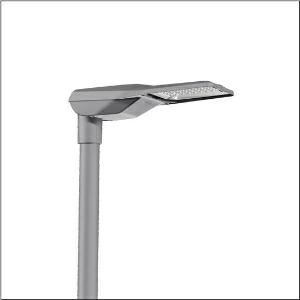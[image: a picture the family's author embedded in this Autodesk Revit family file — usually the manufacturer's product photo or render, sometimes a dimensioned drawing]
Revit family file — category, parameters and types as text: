
# Revit family: streetlight_sl_21_iq_mini___stw1_0a_5xe2e31d08hb_6dd6
name_source: partatom
category: Lighting Fixtures
units: mm (PartAtom-declared; Revit-internal decimal feet)

## family parameters
Cut with Voids When Loaded = No
Host = Face
Light Source = No
Part Type = Normal
Room Calculation Point = No
Round Connector Dimension = Use Diameter
Shared = No

## types (1)
- --- (1 x LED, 9450 lm, 70.9 W, 3000K)
    Apparent Load = 71 VA
    CIE Flux Codes = 38 75 98 100 100
    Color Rendering = 70
    Color Temperature = 3000K
    Default Elevation = 1800 mm
    Description = Streetlight SL 21 iQ mini, mast luminaire, primary light control with lens, of PMMA, primary optical cover: cover, of toughened safety glass, transparent, light distribution: STW1.0a, light emission: direct distribution, primary light characteristic: asymmetric, installation type: post-top, side-entry, LED, High Power LED, rated luminous flux: 9.450lm, luminous efficacy: 133lm/W, light colour: 730, colour temperature: 3000K, control: Auto-Match, Temp-Guard, Lumen-Switch, Night-Set, Smart-Wire, Light-Fading, Desk-Remote (wireless, voltage-free reading and setting of iQ features in the workshop via application-optimized NFC function/RFID function), optimised constant luminous flux control (CLO 2.0), pre-setting: linear dimming characteristic, mains connection: 220..240V, AC, 50/60Hz, start of lifetime: 71W, end of service life: 75W, reduction: 31W, luminaire housing, of diecast aluminium, powder-coated, Siteco® metallic grey (DB 702S), corrosivity category C5 mid according to DIN EN ISO 12944, please order mast flange separately, inclination adjustable: 0°, 5°, 10°, 15°, sealing non-destructively replaceable, multi-level sealing system, length: 628mm, width: 235mm, height: 110mm, mast flange for spigot size: 42mm (side-entry): 5XC10008XM4, 60/48mm (side-entry/post-top): 5XC10108XM2, 76/60mm (side-entry/post-top): 5XC10108XM1, protection rating (complete): IP66, insulation class (complete): insulation class II (safety insulation), certification: CE, ENEC, ENEC+, VDE, impact resistance: IK09, permissible operating ambient temperature for outdoor applications: -40..+50°C, standard-compliant lighting for roads and squares, packaging unit: 1 piece

Light Distribution: STW1.0a
    Height = 110 mm
    Lamp = 1 x LED
    Lamp Light Flux = 9450 lm
    Lamp Power = 70.9 W
    Lamp count = 1
    Length = 625 mm
    Luminous efficacy = 133 lm/W
    Manufacturer = Siteco
    ModVariant = No
    Model = 5XE2E31D08HB
    Number of Poles = 1
    OnlyDefault = Yes
    Power Factor = 1
    Product Name = Streetlight SL 21 iQ mini | STW1.0a
    Product group = mast luminaire | pylon top
    ProductGroupID = 6100
    Protection Class = Protection class II
    Protection Degree = IP 66
    RLX_Detail_Level = 1
    RLX_Emergency_Light_Flux = 0 lm
    RLX_Emergency_Type = 0
    RLX_Emergency_Type_DB = No
    RlxData = <blob elided: 92269 chars, md5=0020da54>
    Socket = socket
    Standby Power = 0 W
    System Light Flux = 9450 lm
    System Power = 71 W
    Type Comments = factory setting: luminous flux: 100 % | dim-lin: 254 | 711 mA
    Type Image = l_1003519.jpg
    URL = http://relux.com
    VarID = @adj_128217
    Voltage = 0 V
    Weight = 0.00 kg
    Width = 234 mm

## geometry (parser evidence)
native form markers: Blend x4, Sweep x10
no freeform markers — native parametric forms only
